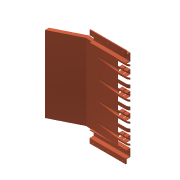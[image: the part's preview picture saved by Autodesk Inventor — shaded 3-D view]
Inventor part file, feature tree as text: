
AUTODESK INVENTOR PART (.ipt)
format: ipt  version: 2015 (Build 190159000, 159)  size: 556,032 bytes
history: native  units: mm
features: sketch x15, extrude x14, pattern_linear x6, other x3, revolve x1
ambient origin geometry x8: Origin, YZ Plane, XZ Plane, XY Plane, X Axis, Y Axis, Z Axis, Center Point
bodies: 实体1 (feature_tree)
feature tree (39):
  extrude  "拉伸1"  Depth=15.12mm
  extrude  "拉伸2"  Depth=2.0mm
  extrude  "拉伸3"  Depth=20.0mm
  pattern_linear  "矩形阵列1"  Count1=6  [1 undecoded]
  extrude  "拉伸4"  Depth=480.0mm TaperAngle=0.0deg
  extrude  "拉伸5"  Depth=20.0mm
  pattern_linear  "矩形阵列2"  Count1=4  [1 undecoded]
  extrude  "拉伸6"  Depth=81.504mm
  extrude  "拉伸8"  Depth=10.0mm
  extrude  "拉伸9"  Depth=10.0mm
  pattern_linear  "矩形阵列3"  Count1=3  [1 undecoded]
  extrude  "拉伸10"  Depth=10.0mm
  pattern_linear  "矩形阵列4"  Count1=5 Spacing1=0.0mm
  extrude  "拉伸11"  Depth=20.0mm
  extrude  "拉伸12"  Depth=50.0mm TaperAngle=0.0deg
  other  "工作轴1"
  revolve  "旋转1"  [1 undecoded]
  extrude  "拉伸13"  Depth=4.0mm
  extrude  "拉伸14"  Depth=4.0mm
  pattern_linear  "矩形阵列5"  Spacing1=4.0mm  [1 undecoded]
  extrude  "拉伸15"  Depth=4.0mm
  pattern_linear  "矩形阵列6"  Count1=4  [1 undecoded]
  other  "加厚1"
  other  "加厚2"
  sketch  "草图1"  dims[d0=3.335281mm d1=15.12mm]
  sketch  "草图2"  dims[d2=2.0mm d3=213.363mm]
  sketch  "草图3"  dims[d4=480.0mm d5=0.0mm d6=20.0mm d7=60.0mm]
  sketch  "草图4"  dims[d8=2.0mm d9=480.0mm d10=0.0mm]
  sketch  "草图5"  dims[d11=20.0mm d12=20.0mm]
  sketch  "草图6"  dims[d13=0.0mm d14=40.0mm d16=120.0mm]
  sketch  "草图8"  dims[d17=164.137mm d18=81.504mm]
  sketch  "草图9"  dims[d19=480.0mm d20=0.0mm d21=10.0mm]
  sketch  "草图10"  dims[d22=2.005016mm d23=10.0mm d24=30.0mm]
  sketch  "草图11"  dims[d25=2.0mm d26=10.0mm]
  sketch  "草图12"  dims[d27=2.0mm d28=50.0mm d29=0.0mm]
  sketch  "草图13"  dims[d30=40.0mm d32=120.0mm d33=20.0mm]
  sketch  "草图14"  dims[d34=110.0mm d35=50.0mm d36=0.0mm]
  sketch  "草图15"  dims[d42=10.0mm d43=10.0mm]
  sketch  "草图16"  dims[d44=50.0mm d45=0.0mm d46=4.0mm d47=4.0mm d48=4.0mm d49=4.0mm d50=40.0mm d51=30.0mm d52=2.5mm d53=4.0mm d54=4.0mm d55=4.0mm d56=4.0mm d57=40.0mm d58=2.5mm d59=30.0mm d60=227.5mm d61=0.0mm d62=30.0mm d64=120.0mm d65=20.0mm d66=20.0mm d67=4.0mm d68=0.0mm d69=20.0mm d71=476.0mm d72=8.0mm d73=8.0mm d74=8.0mm d75=8.0mm d76=8.0mm d77=8.0mm d78=13.0mm d79=20.0mm d80=13.0mm d81=13.0mm d82=20.0mm d83=113.75mm d84=20.0mm d85=13.0mm d86=13.0mm d87=13.0mm d88=113.75mm d89=20.0mm d90=4.0mm d91=0.0mm d92=2.5mm d93=7.0mm d94=20.0mm d95=25.0mm d96=13.0mm d97=10.0mm d98=0.0mm d99=10.0mm d100=20.0mm d101=10.0mm d102=2.005016mm d103=45.0deg d104=10.0mm d105=480.0mm d106=0.0mm d107=4.0mm d108=0.0mm d109=20.0mm d111=476.0mm d112=5.0mm d113=5.0mm d114=5.0mm d115=14.0mm d116=7.5mm d117=7.5mm d118=4.0mm d119=0.0mm d120=20.0mm d122=476.0mm d123=1.704mm d124=1.704mm d125=1.704mm d126=1.704mm]
note: 6 required parameter values undecoded (feature->parameter linkage not recoverable at this tier; creation-order binding heuristic only, values carry confidence <= 0.55)